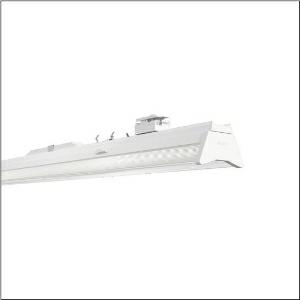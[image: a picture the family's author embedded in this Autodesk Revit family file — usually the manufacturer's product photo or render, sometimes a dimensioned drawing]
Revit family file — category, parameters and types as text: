
# Revit family: licross_r__21_performance_mo_52tm167n46xg_7cd2
name_source: partatom
category: Lighting Fixtures
units: mm (PartAtom-declared; Revit-internal decimal feet)

## family parameters
Cut with Voids When Loaded = No
Host = Face
Light Source = No
Part Type = Normal
Room Calculation Point = No
Round Connector Dimension = Use Diameter
Shared = No

## types (1)
- Licross® 21 Performance MO (1 x LED, 6000 lm, 32.4 W, 4000K)
    Apparent Load = 32 VA
    CIE Flux Codes = 66 88 96 79 100
    Color Rendering = 80
    Color Temperature = 4000K
    Default Elevation = 1800 mm
    Description = Licross® 21 Performance MO, luminaire insert, of sheet steel, galvanised, coil coated, white, length: 1.500mm, width: 120mm, height: 123mm, LED rated luminous flux: 6.000lm, light colour: 840, control gear: ON/OFF, with plug, 3-pole, with phase selection, mains connection: 220..240V, AC, 50/60Hz, rated input power: 32W, internal wiring halogen-free, primary light control with lens, of plastic, primary optical cover: cover, of PMMA, light emission: direct/indirect distribution, primary light characteristic: symmetric, protection rating (complete): IP40, insulation class (complete): insulation class I (protective earthing), certification: CE, ENEC, UKCA, protection symbol: D if used in an environment without relevant dust loads with corresponding accessories, impact resistance: IK06, permissible ambient temperature for indoor applications: -35..+50°C, corresponds to IFS (International Featured Standards) requirements for safety and quality in the food industry, reducing of maximum allowable ambient temperature of 5°C with ceiling mounting, LABS conformity tested according to VDMA 24364:2018-05, packaging unit: 1 piece
    Height = 114 mm
    Lamp = 1 x LED
    Lamp Light Flux = 6000 lm
    Lamp Power = 32.4 W
    Lamp count = 1
    Length = 1500 mm
    Luminous efficacy = 185 lm/W
    Manufacturer = Siteco
    ModVariant = No
    Model = 52TM167N46XG
    Mounting Place = Ceiling
    Mounting Type = Pendant
    Number of Poles = 1
    OnlyDefault = Yes
    Power Factor = 1
    Product Name = Licross® 21 Performance MO
    Product group = luminaire insert | ceiling pendant
    ProductGroupID = 902
    Protection Class = Protection class I
    Protection Degree = IP 40
    RLX_Detail_Level = 1
    RLX_Emergency_Light_Flux = 0 lm
    RLX_Emergency_Type = 0
    RLX_Emergency_Type_DB = No
    RlxData = <blob elided: 30397 chars, md5=db7f4584>
    Socket = socket
    Standby Power = 0 W
    System Light Flux = 6000 lm
    System Power = 32 W
    Type Comments = Product without accessories
    Type Image = l_1256138.jpg
    URL = http://relux.com
    VarID = ---
    Voltage = 0 V
    Weight = 0.00 kg
    Width = 120 mm

## geometry (parser evidence)
native form markers: Blend x4, Sweep x14
no freeform markers — native parametric forms only
